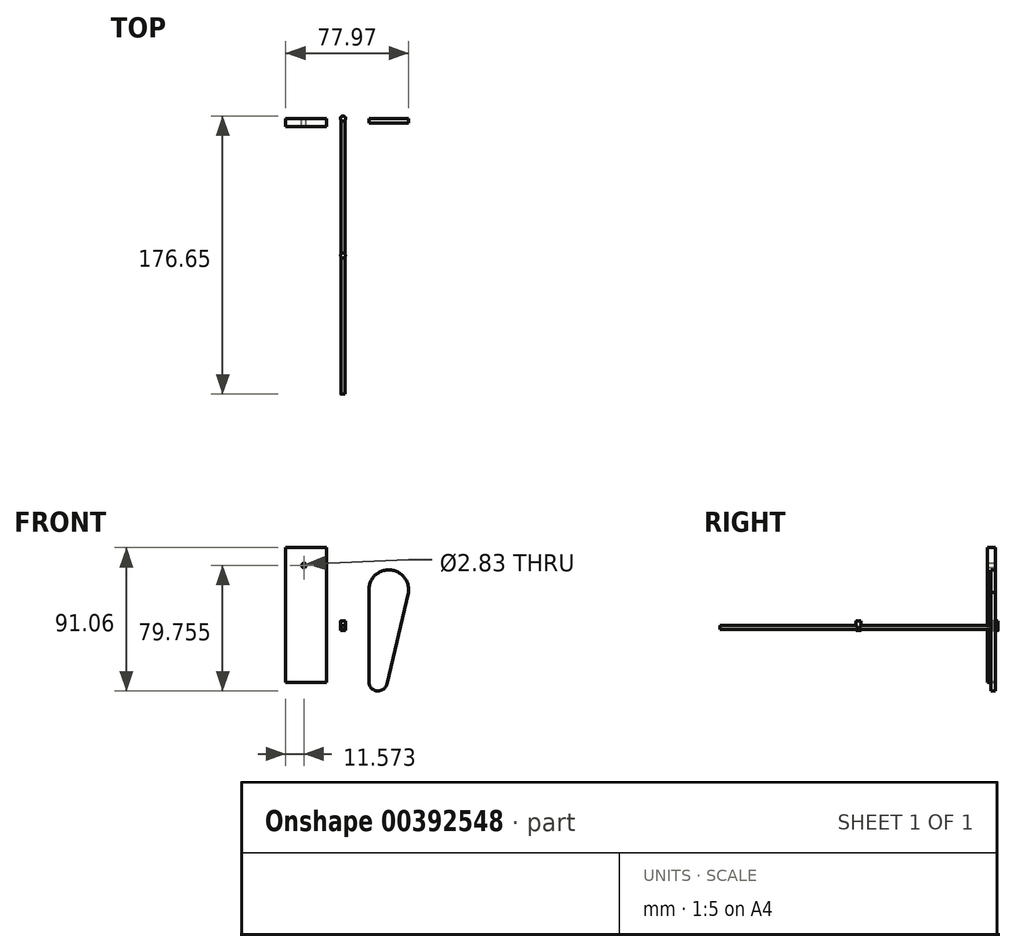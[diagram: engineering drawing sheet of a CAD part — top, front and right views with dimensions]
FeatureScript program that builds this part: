
annotation { "Feature Type Name" : "Feature", "Feature Type Description" : "" }
export const myFeature = defineFeature(function(context is Context, id is Id, definition is map)
    precondition{}
    {
        {
            var Q0;
            Q0=qCreatedBy(makeId("Front.planeOp"),FACE);
            var sketch = newSketch(context, id + "F0", { "sketchPlane" : qUnion([Q0])});
            skCircle(sketch, "E0", {"center": v(14.14, -38.6) * mm, "radius": 5.8 * mm});
            skCircle(sketch, "E1", {"center": v(20.95, 19.95) * mm, "radius": 12.57 * mm});
            skLineSegment(sketch, "E2", {"start": v(8.35, -38.4) * mm, "end": v(8.38, 19.96) * mm});
            skLineSegment(sketch, "E3", {"start": v(33.4, 18.11) * mm, "end": v(19.77, -39.92) * mm});
            skCircle(sketch, "E4", {"center": v(-8.09, -4.13) * mm, "radius": 1.3 * mm});
            skLineSegment(sketch, "E5.bottom", {"start": v(-44.44, 46.67) * mm, "end": v(-18.67, 46.67) * mm});
            skLineSegment(sketch, "E5.top", {"start": v(-44.44, -39.05) * mm, "end": v(-18.67, -39.05) * mm});
            skLineSegment(sketch, "E5.left", {"start": v(-44.44, 46.67) * mm, "end": v(-44.44, -39.05) * mm});
            skLineSegment(sketch, "E5.right", {"start": v(-18.67, 46.67) * mm, "end": v(-18.67, -39.05) * mm});
            skCircle(sketch, "E6", {"center": v(-32.87, 35.37) * mm, "radius": 1.42 * mm});
            skSolve(sketch);
        }
        {
            var Q0;
            {var subQ0=sQuery(id+"F0.wireOp",EDGE,"E1");var subQ1=makeQuery(id+"F0.imprint","INTERSECT",VERTEX,{"derivedFrom":[subQ0,sQuery(id+"F0.wireOp",EDGE,"E2")]});Q0=makeQuery(id+"F0.imprint","IMPRINT",FACE,{"disambiguationData":[TD([[makeQuery(id+"F0.imprint","IMPRINT",EDGE,{"disambiguationData":[TD([[subQ1,-1.0]])],"derivedFrom":subQ0}),1.0]])]});}
            var Q1;
            {var subQ0=sQuery(id+"F0.wireOp",EDGE,"E2");Q1=makeQuery(id+"F0.imprint","IMPRINT",FACE,{"disambiguationData":[TD([[makeQuery(id+"F0.imprint","IMPRINT",EDGE,{"derivedFrom":subQ0}),-1.0]])]});}
            var Q2;
            {var subQ0=sQuery(id+"F0.wireOp",EDGE,"E0");var subQ1=makeQuery(id+"F0.imprint","INTERSECT",VERTEX,{"derivedFrom":[subQ0,sQuery(id+"F0.wireOp",EDGE,"E2")]});Q2=makeQuery(id+"F0.imprint","IMPRINT",FACE,{"disambiguationData":[TD([[makeQuery(id+"F0.imprint","IMPRINT",EDGE,{"disambiguationData":[TD([[subQ1,-1.0]])],"derivedFrom":subQ0}),1.0]])]});}
            extrude(context, id + "F1", {"entities" : qUnion([Q0, Q1, Q2]), "depth" : 3 * mm});
        }
        {
            var Q0;
            Q0=makeQuery(id+"F0.imprint","IMPRINT",FACE,{"disambiguationData":[TD([[makeQuery(id+"F0.imprint","IMPRINT",EDGE,{"derivedFrom":sQuery(id+"F0.wireOp",EDGE,"E4")}),1.0]])]});
            extrude(context, id + "F2", {"entities" : qUnion([Q0]), "depth" : 175 * mm});
        }
        {
            var Q0;
            Q0=makeQuery(id+"F0.imprint","IMPRINT",FACE,{"disambiguationData":[TD([[makeQuery(id+"F0.imprint","IMPRINT",EDGE,{"derivedFrom":sQuery(id+"F0.wireOp",EDGE,"E5.bottom")}),-1.0]])]});
            extrude(context, id + "F3", {"entities" : qUnion([Q0]), "depth" : 5 * mm});
        }
        {
            var Q0;
            Q0=qCreatedBy(makeId("Top.planeOp"),FACE);
            var sketch = newSketch(context, id + "F4", { "sketchPlane" : qUnion([Q0])});
            skCircle(sketch, "E7", {"center": v(-8.05, 0) * mm, "radius": 1.65 * mm});
            skCircle(sketch, "E8", {"center": v(-8.07, -86.98) * mm, "radius": 1.52 * mm});
            skSolve(sketch);
        }
        {
            var Q0;
            Q0=makeQuery(id+"F4.imprint","IMPRINT",FACE,{"disambiguationData":[TD([[makeQuery(id+"F4.imprint","IMPRINT",EDGE,{"derivedFrom":sQuery(id+"F4.wireOp",EDGE,"E7")}),1.0]])]});
            var Q1;
            Q1=makeQuery(id+"F4.imprint","IMPRINT",FACE,{"disambiguationData":[TD([[makeQuery(id+"F4.imprint","IMPRINT",EDGE,{"derivedFrom":sQuery(id+"F4.wireOp",EDGE,"E8")}),1.0]])]});
            extrude(context, id + "F5", {"entities" : qUnion([Q0, Q1]), "operationType" : NewBodyOperationType.ADD, "oppositeDirection" : true, "depth" : 6 * mm});
        }
    });
